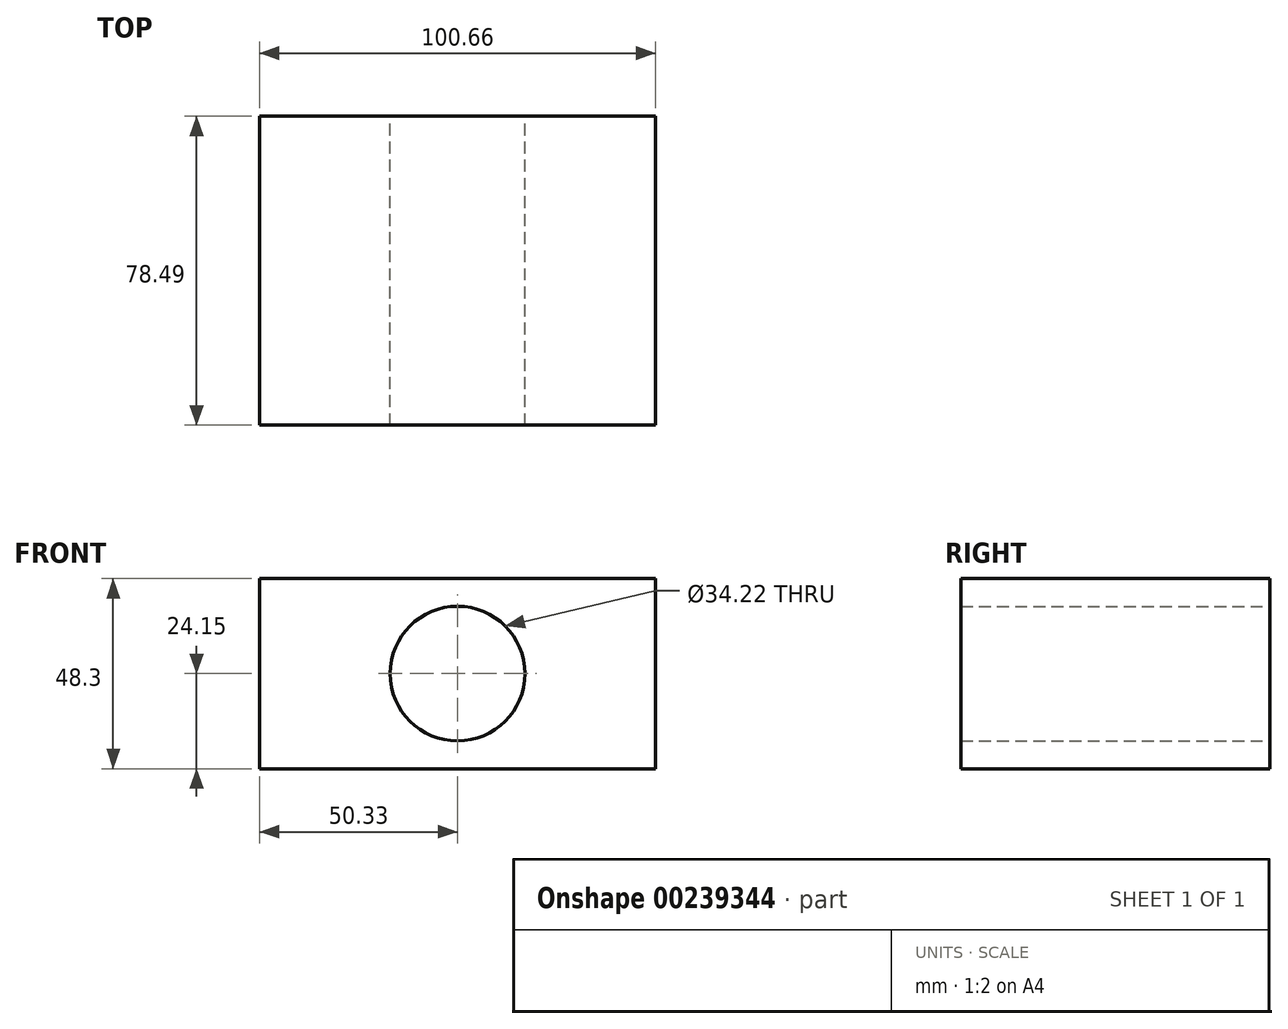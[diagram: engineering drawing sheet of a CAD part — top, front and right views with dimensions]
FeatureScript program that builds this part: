
annotation { "Feature Type Name" : "Feature", "Feature Type Description" : "" }
export const myFeature = defineFeature(function(context is Context, id is Id, definition is map)
    precondition{}
    {
        {
            var Q0;
            Q0=qCreatedBy(makeId("Front.planeOp"),FACE);
            var sketch = newSketch(context, id + "F0", { "sketchPlane" : qUnion([Q0])});
            skLineSegment(sketch, "E0.bottom", {"start": v(50.33, 24.15) * mm, "end": v(-50.33, 24.15) * mm});
            skLineSegment(sketch, "E0.top", {"start": v(50.33, -24.15) * mm, "end": v(-50.33, -24.15) * mm});
            skLineSegment(sketch, "E0.left", {"start": v(50.33, 24.15) * mm, "end": v(50.33, -24.15) * mm});
            skLineSegment(sketch, "E0.right", {"start": v(-50.33, 24.15) * mm, "end": v(-50.33, -24.15) * mm});
            skPoint(sketch, "E0.middle", {"position": v(0, 0) * mm});
            skCircle(sketch, "E1", {"center": v(0, 0) * mm, "radius": 17.1 * mm});
            skSolve(sketch);
        }
        {
            var Q0;
            Q0 = qSketchRegion(id + "F0", true);
            extrude(context, id + "F1", {"entities" : qUnion([Q0]), "depth" : 78.49 * mm});
        }
    });
